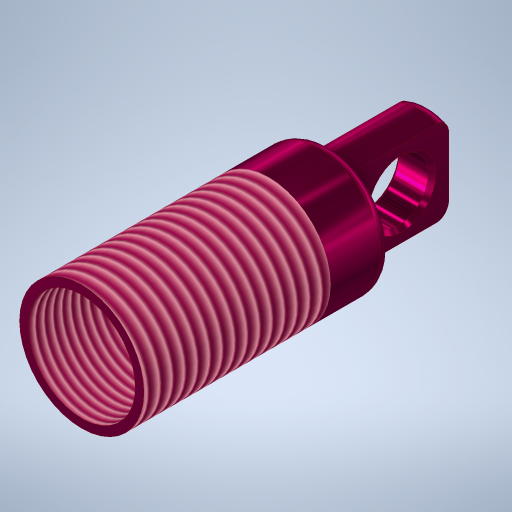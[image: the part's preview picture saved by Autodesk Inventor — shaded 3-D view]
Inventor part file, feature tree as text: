
AUTODESK INVENTOR PART (.ipt)
format: ipt  version: 2023.1 (Build 271208000, 208)  size: 429,056 bytes
history: native  units: in
note: dims shown in document units (in); Inventor stores cm internally (conversion verified against a paired STEP export)
features: extrude x4, sketch x4, fillet x2, thread x2, shell x1, chamfer x1, projected_geometry x1
ambient origin geometry x8: Origin, YZ Plane, XZ Plane, XY Plane, X Axis, Y Axis, Z Axis, Center Point
bodies: Solid1 (feature_tree)
feature tree (15):
  extrude  "Extrusion1"  Depth=0.05in TaperAngle=0.0deg
  shell  "Shell1"  Thickness=0.035in
  fillet  "Fillet1"  Radius=0.05in
  extrude  "Extrusion2"  Depth=0.4in TaperAngle=0.0deg
  extrude  "Extrusion3"  Depth=0.4in TaperAngle=0.0deg
  extrude  "Extrusion4"  Depth=0.05in
  chamfer  "Chamfer1"  [1 undecoded]
  fillet  "Fillet2"  Radius=0.015in
  thread  "Thread1"  [1 undecoded]
  thread  "Thread2"  [1 undecoded]
  sketch  "Sketch1"  dims[d0=0.5in d1=1.0in d2=0.0in d3=0.035in d4=0.05in]
  sketch  "Sketch2"  dims[d5=0.375in d6=0.4in d7=0.0in]
  sketch  "Sketch3"  dims[d8=0.15in d9=0.4in d10=0.0in]
  sketch  "Sketch4"  dims[d11=0.24in d12=0.1875in d13=0.0in d14=0.0in d15=0.015in d16=0.125in d17=45.0deg d18=0.05in d19=0.75in d20=0.0in d21=0.375in d22=0.0in]
  projected_geometry  "Project Cut Edges1"
note: 3 required parameter values undecoded (feature->parameter linkage not recoverable at this tier; creation-order binding heuristic only, values carry confidence <= 0.55)
